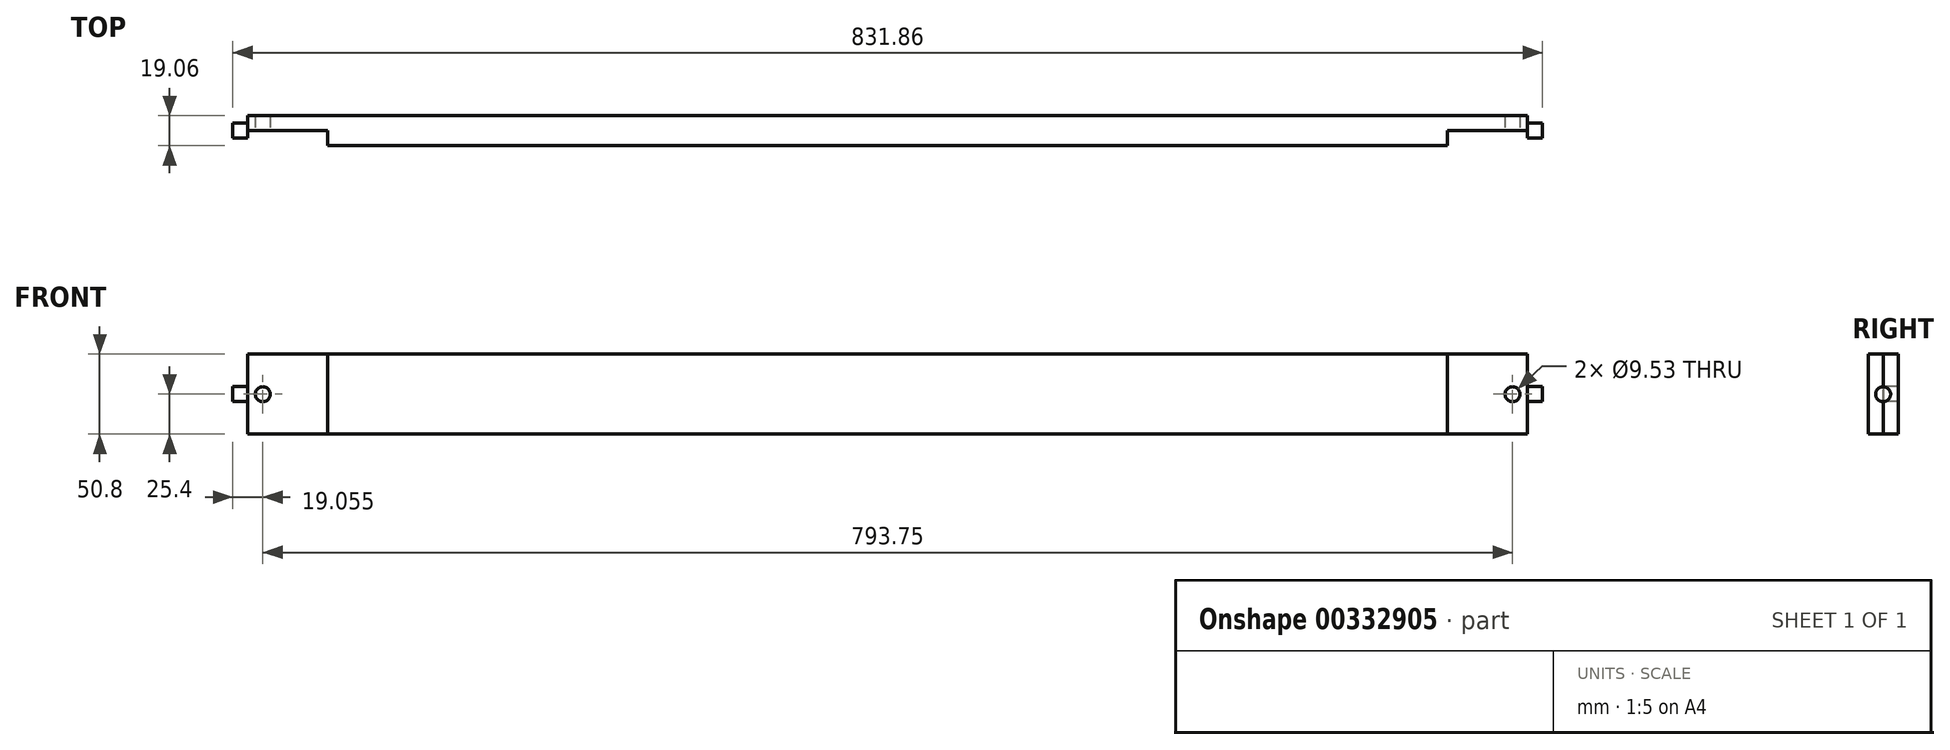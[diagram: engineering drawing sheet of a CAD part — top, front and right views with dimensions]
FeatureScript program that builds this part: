
annotation { "Feature Type Name" : "Feature", "Feature Type Description" : "" }
export const myFeature = defineFeature(function(context is Context, id is Id, definition is map)
    precondition{}
    {
        {
            var Q0;
            Q0=qCreatedBy(makeId("Top.planeOp"),FACE);
            var sketch = newSketch(context, id + "F0", { "sketchPlane" : qUnion([Q0])});
            skLineSegment(sketch, "E0.bottom", {"start": v(-355.6, -9.53) * mm, "end": v(355.6, -9.53) * mm});
            skLineSegment(sketch, "E0.top", {"start": v(-406.4, 9.53) * mm, "end": v(406.4, 9.53) * mm});
            skLineSegment(sketch, "E0.left", {"start": v(-406.4, 0) * mm, "end": v(-406.4, 9.53) * mm});
            skLineSegment(sketch, "E0.right", {"start": v(406.4, 0) * mm, "end": v(406.4, 9.52) * mm});
            skPoint(sketch, "E0.middle", {"position": v(0, 0) * mm});
            skLineSegment(sketch, "E1.top", {"start": v(-406.4, 0) * mm, "end": v(-355.6, 0) * mm});
            skLineSegment(sketch, "E1.right", {"start": v(-355.6, -9.53) * mm, "end": v(-355.6, 0) * mm});
            skLineSegment(sketch, "E2.top", {"start": v(406.4, 0) * mm, "end": v(355.6, 0) * mm});
            skLineSegment(sketch, "E2.right", {"start": v(355.6, -9.53) * mm, "end": v(355.6, 0) * mm});
            skPoint(sketch, "E3.orphan", {"position": v(-406.4, -9.53) * mm});
            skPoint(sketch, "E4.orphan", {"position": v(406.4, -9.53) * mm});
            skSolve(sketch);
        }
        {
            var Q0;
            Q0=qSketchRegion(id+"F0",true);
            extrude(context, id + "F1", {"entities" : qUnion([Q0]), "depth" : 50.8 * mm});
        }
        {
            var Q0;
            Q0=qCreatedBy(makeId("Right.planeOp"),FACE);
            cPlane(context, id + "F2", {"entities" : qUnion([Q0]), "cplaneType" : CPlaneType.OFFSET, "offset" : 406.4 * mm, "width" : 152.4 * mm, "height" : 152.4 * mm});
        }
        {
            var Q0;
            Q0=qCreatedBy(id+"F2.planeOp",FACE);
            var sketch = newSketch(context, id + "F3", { "sketchPlane" : qUnion([Q0])});
            skCircle(sketch, "E5", {"center": v(0, 25.4) * mm, "radius": 4.76 * mm});
            skSolve(sketch);
        }
        {
            var Q0;
            Q0=qSketchRegion(id+"F3",true);
            extrude(context, id + "F4", {"entities" : qUnion([Q0]), "operationType" : NewBodyOperationType.ADD, "depth" : 9.52 * mm});
        }
        {
            var Q0;
            Q0=qCreatedBy(makeId("Right.planeOp"),FACE);
            cPlane(context, id + "F5", {"entities" : qUnion([Q0]), "cplaneType" : CPlaneType.OFFSET, "offset" : 406.4 * mm, "oppositeDirection" : true, "width" : 152.4 * mm, "height" : 152.4 * mm});
        }
        {
            var Q0;
            Q0=qCreatedBy(id+"F5.planeOp",FACE);
            var sketch = newSketch(context, id + "F6", { "sketchPlane" : qUnion([Q0])});
            skCircle(sketch, "E6", {"center": v(0, 25.42) * mm, "radius": 4.76 * mm});
            skSolve(sketch);
        }
        {
            var Q0;
            Q0=qSketchRegion(id+"F6",true);
            extrude(context, id + "F7", {"entities" : qUnion([Q0]), "operationType" : NewBodyOperationType.ADD, "oppositeDirection" : true, "depth" : 9.52 * mm});
        }
        {
            var Q0;
            Q0=qCreatedBy(makeId("Front.planeOp"),FACE);
            var sketch = newSketch(context, id + "F8", { "sketchPlane" : qUnion([Q0])});
            skCircle(sketch, "E7", {"center": v(-396.88, 25.4) * mm, "radius": 4.76 * mm});
            skCircle(sketch, "E8", {"center": v(396.88, 25.4) * mm, "radius": 4.76 * mm});
            skSolve(sketch);
        }
        {
            var Q0;
            Q0 = qSketchRegion(id + "F8", true);
            extrude(context, id + "F9", {"entities" : qUnion([Q0]), "operationType" : NewBodyOperationType.REMOVE, "oppositeDirection" : true, "depth" : 25.4 * mm});
        }
    });
